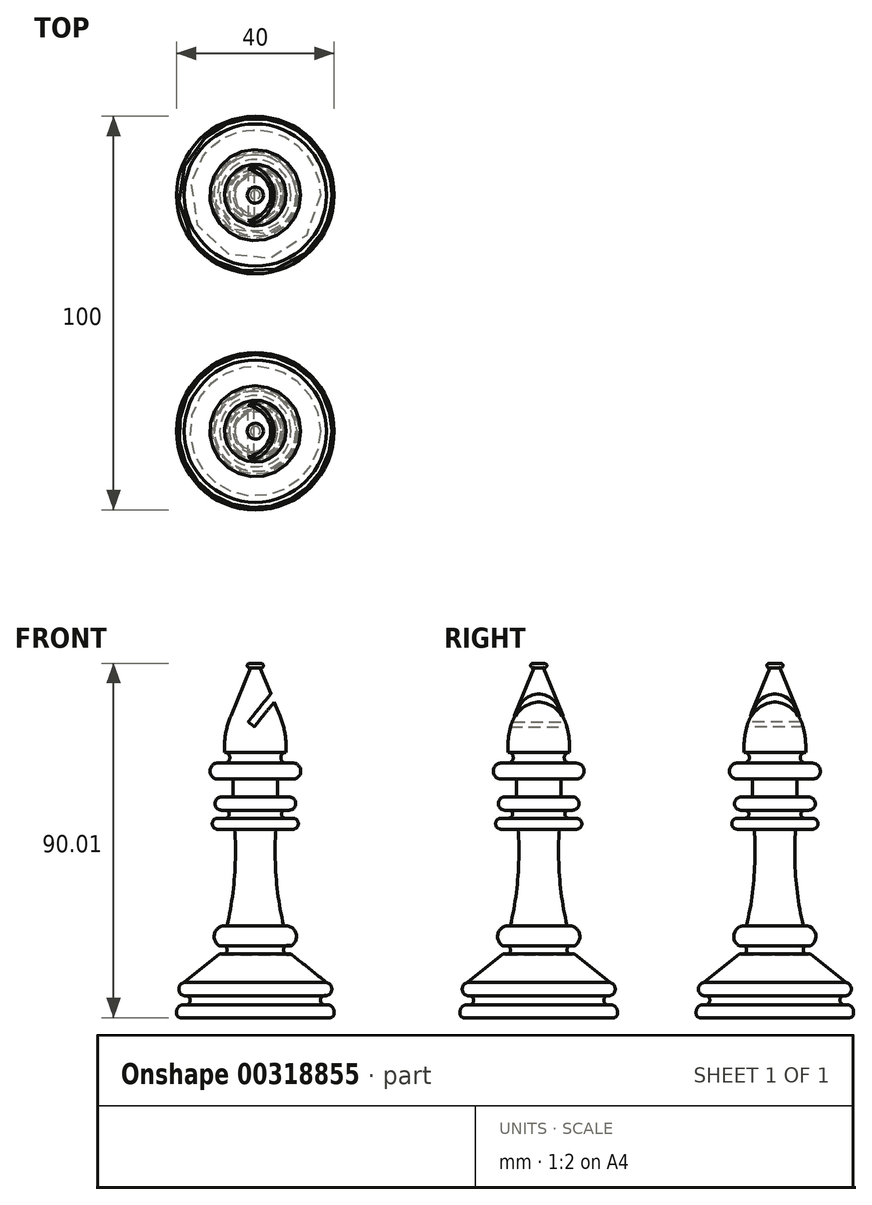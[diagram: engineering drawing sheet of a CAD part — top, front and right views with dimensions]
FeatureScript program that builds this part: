
annotation { "Feature Type Name" : "Feature", "Feature Type Description" : "" }
export const myFeature = defineFeature(function(context is Context, id is Id, definition is map)
    precondition{}
    {
        {
            var Q0;
            Q0=qCreatedBy(makeId("Front.planeOp"),FACE);
            var sketch = newSketch(context, id + "F0", { "sketchPlane" : qUnion([Q0])});
            skLineSegment(sketch, "E0", {"start": v(0, 45) * mm, "end": v(0, -45) * mm});
            skLineSegment(sketch, "E1", {"start": v(0, -45) * mm, "end": v(-20, -45) * mm});
            skLineSegment(sketch, "E2", {"start": v(-20, -45) * mm, "end": v(-20, -43.5) * mm});
            skArc(sketch, "E3", {"start": v(-18.08, -41.7) * mm, "mid": v(-19.43, -42.18) * mm, "end": v(-20, -43.5) * mm});
            skArc(sketch, "E4", {"start": v(-18.08, -41.7) * mm, "mid": v(-16.53, -40.56) * mm, "end": v(-18.08, -39.43) * mm});
            skArc(sketch, "E5", {"start": v(-18.08, -36.04) * mm, "mid": v(-19.44, -37.74) * mm, "end": v(-18.08, -39.43) * mm});
            skLineSegment(sketch, "E6", {"start": v(-18.08, -36.04) * mm, "end": v(-9.04, -28.81) * mm});
            skArc(sketch, "E7", {"start": v(-9.04, -28.81) * mm, "mid": v(-7.18, -27.8) * mm, "end": v(-9.04, -26.78) * mm});
            skArc(sketch, "E8", {"start": v(-7.2, -21.7) * mm, "mid": v(-10.3, -23.45) * mm, "end": v(-9.04, -26.78) * mm});
            skArc(sketch, "E9", {"start": v(-7.2, -21.7) * mm, "mid": v(-5.3, -9.48) * mm, "end": v(-5.22, 2.87) * mm});
            skLineSegment(sketch, "E10", {"start": v(-5.22, 2.87) * mm, "end": v(-9.54, 2.87) * mm});
            skArc(sketch, "E11", {"start": v(-9.54, 5.68) * mm, "mid": v(-10.94, 4.27) * mm, "end": v(-9.54, 2.87) * mm});
            skLineSegment(sketch, "E12", {"start": v(-9.54, 5.68) * mm, "end": v(-7.63, 5.68) * mm});
            skArc(sketch, "E13", {"start": v(-7.63, 5.68) * mm, "mid": v(-6.61, 6.7) * mm, "end": v(-7.63, 7.71) * mm});
            skLineSegment(sketch, "E14", {"start": v(-7.63, 7.71) * mm, "end": v(-8.58, 7.71) * mm});
            skPoint(sketch, "E14.endSnap0", {"position": v(-8.58, 5.68) * mm});
            skArc(sketch, "E15", {"start": v(-8.58, 11.07) * mm, "mid": v(-10.27, 9.4) * mm, "end": v(-8.58, 7.71) * mm});
            skLineSegment(sketch, "E16", {"start": v(-8.58, 11.07) * mm, "end": v(-5.65, 11.07) * mm});
            skLineSegment(sketch, "E17", {"start": v(-5.65, 11.07) * mm, "end": v(-5.65, 15.6) * mm});
            skLineSegment(sketch, "E18", {"start": v(-5.65, 15.6) * mm, "end": v(-9.5, 15.6) * mm});
            skArc(sketch, "E19", {"start": v(-9.5, 19.7) * mm, "mid": v(-11.54, 17.66) * mm, "end": v(-9.5, 15.6) * mm});
            skLineSegment(sketch, "E20", {"start": v(-9.5, 19.7) * mm, "end": v(-7.83, 19.7) * mm});
            skArc(sketch, "E21", {"start": v(-7.83, 19.7) * mm, "mid": v(-6.47, 21.07) * mm, "end": v(-7.83, 22.44) * mm});
            skLineSegment(sketch, "E22", {"start": v(-6.23, 31.7) * mm, "end": v(-1.2, 43.95) * mm});
            skArc(sketch, "E23", {"start": v(-6.23, 31.7) * mm, "mid": v(-7.54, 27.16) * mm, "end": v(-7.83, 22.44) * mm});
            skLineSegment(sketch, "E24", {"start": v(0, 73.1) * mm, "end": v(0, -70.16) * mm, "construction": true});
            skLineSegment(sketch, "E25", {"start": v(-1.48, 45.01) * mm, "end": v(0, 45) * mm});
            skArc(sketch, "E26", {"start": v(-1.48, 45.01) * mm, "mid": v(-2.03, 44.3) * mm, "end": v(-1.2, 43.95) * mm});
            skSolve(sketch);
        }
        {
            var Q0;
            Q0=makeQuery(id+"F0.imprint","IMPRINT",FACE,{"disambiguationData":[TD([[makeQuery(id+"F0.imprint","IMPRINT",EDGE,{"derivedFrom":sQuery(id+"F0.wireOp",EDGE,"E0")}),-1.0]])]});
            var Q1;
            Q1=sQuery(id+"F0.wireOp",EDGE,"E24");
            revolve(context, id + "F1", {"entities" : qUnion([Q0]), "axis" : qUnion([Q1]), "revolveType" : RevolveType.FULL});
        }
        {
            var Q0;
            Q0=makeQuery(id+"F1.opRevolve","SWEPT_EDGE",EDGE,{"disambiguationData":[OSD([sQuery(id+"F0.wireOp",EDGE,"E1"),sQuery(id+"F0.wireOp",EDGE,"E2")])]});
            fillet(context, id + "F2", {"entities" : qUnion([Q0]), "radius" : 1 * mm, "tangentPropagation" : true, "allowEdgeOverflow" : false});
        }
        {
            var Q0;
            Q0=qCreatedBy(makeId("Front.planeOp"),FACE);
            var sketch = newSketch(context, id + "F3", { "sketchPlane" : qUnion([Q0])});
            skLineSegment(sketch, "E27", {"start": v(5.88, 39.66) * mm, "end": v(-1.8, 30.17) * mm});
            skLineSegment(sketch, "E28", {"start": v(-1.8, 30.17) * mm, "end": v(-0.27, 28.92) * mm});
            skLineSegment(sketch, "E29", {"start": v(-0.27, 28.92) * mm, "end": v(7.42, 38.43) * mm});
            skLineSegment(sketch, "E30", {"start": v(7.42, 38.43) * mm, "end": v(5.88, 39.66) * mm});
            skSolve(sketch);
        }
        {
            var Q0;
            Q0=makeQuery(id+"F3.imprint","IMPRINT",FACE,{"disambiguationData":[TD([[makeQuery(id+"F3.imprint","IMPRINT",EDGE,{"derivedFrom":sQuery(id+"F3.wireOp",EDGE,"E27")}),1.0]])]});
            extrude(context, id + "F4", {"entities" : qUnion([Q0]), "operationType" : NewBodyOperationType.REMOVE, "endBound" : BoundingType.SYMMETRIC, "oppositeDirection" : true, "depth" : 25 * mm});
        }
        {
            var Q0;
            Q0=qCreatedBy(makeId("Front.planeOp"),FACE);
            cPlane(context, id + "F5", {"entities" : qUnion([Q0]), "cplaneType" : CPlaneType.OFFSET, "offset" : 30 * mm, "width" : 150 * mm, "height" : 150 * mm});
        }
        {
            var Q0;
            Q0=makeQuery(id+"F1.opRevolve","SWEPT_BODY",BODY,{"disambiguationData":[OSD([sQuery(id+"F0.wireOp",EDGE,"E0"),sQuery(id+"F0.wireOp",EDGE,"E1"),sQuery(id+"F0.wireOp",EDGE,"E2"),sQuery(id+"F0.wireOp",EDGE,"E3"),sQuery(id+"F0.wireOp",EDGE,"E4"),sQuery(id+"F0.wireOp",EDGE,"E5"),sQuery(id+"F0.wireOp",EDGE,"E6"),sQuery(id+"F0.wireOp",EDGE,"E7"),sQuery(id+"F0.wireOp",EDGE,"E8"),sQuery(id+"F0.wireOp",EDGE,"E9"),sQuery(id+"F0.wireOp",EDGE,"E10"),sQuery(id+"F0.wireOp",EDGE,"E11"),sQuery(id+"F0.wireOp",EDGE,"E12"),sQuery(id+"F0.wireOp",EDGE,"E13"),sQuery(id+"F0.wireOp",EDGE,"E14"),sQuery(id+"F0.wireOp",EDGE,"E15"),sQuery(id+"F0.wireOp",EDGE,"E16"),sQuery(id+"F0.wireOp",EDGE,"E17"),sQuery(id+"F0.wireOp",EDGE,"E18"),sQuery(id+"F0.wireOp",EDGE,"E19"),sQuery(id+"F0.wireOp",EDGE,"E20"),sQuery(id+"F0.wireOp",EDGE,"E21"),sQuery(id+"F0.wireOp",EDGE,"E22"),sQuery(id+"F0.wireOp",EDGE,"E23"),sQuery(id+"F0.wireOp",EDGE,"E25"),sQuery(id+"F0.wireOp",EDGE,"E26")])]});
            var Q1;
            Q1=qCreatedBy(id+"F5.planeOp",FACE);
            mirror(context, id + "F6", {"entities" : qUnion([Q0]), "mirrorPlane" : qUnion([Q1])});
        }
    });
